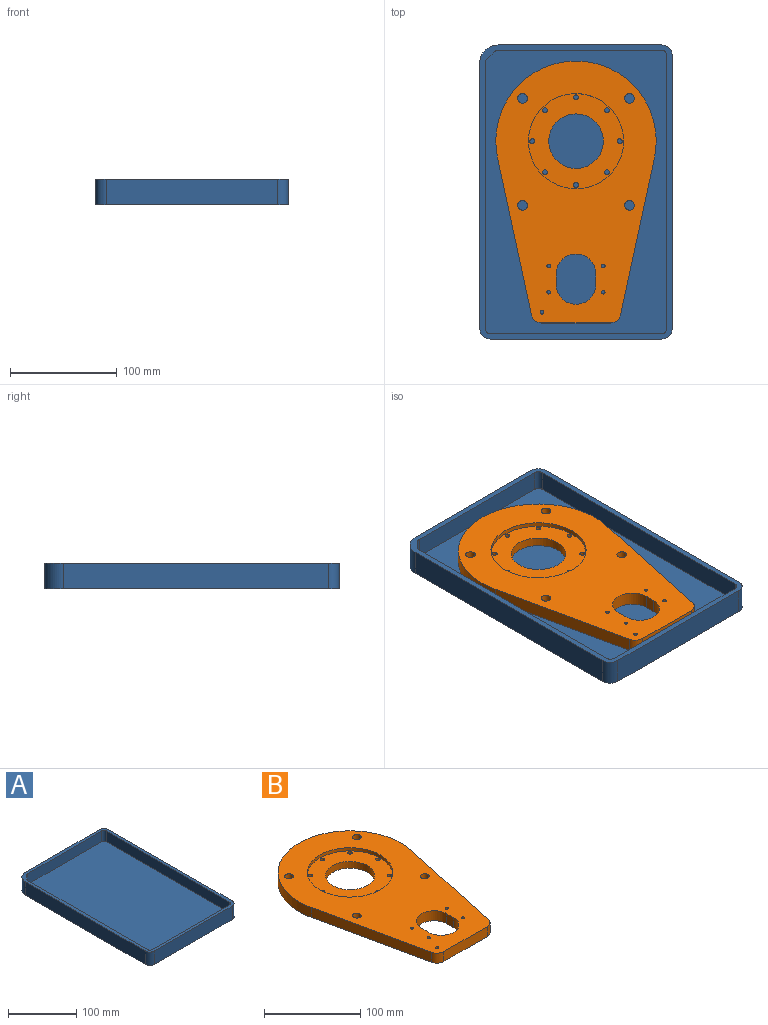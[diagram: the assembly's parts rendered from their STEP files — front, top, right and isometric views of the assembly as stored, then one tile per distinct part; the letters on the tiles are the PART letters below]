
ASSEMBLY  parts=2 mates=1
PART A: 21 faces, bbox 180x275x24 mm
  f0: plane 160x24mm, normal (0,-1,0), area 3840mm2, adj f1,f17,f18,f19
  f1: cylinder r=10mm len=24mm, axis (0,0,-1), area 377mm2, adj f0,f2,f18,f19
  f2: plane 255x24mm, normal (1,0,0), area 6120mm2, adj f1,f3,f18,f19
  f3: cylinder r=10mm len=24mm, axis (0,0,-1), area 377mm2, adj f2,f4,f18,f19
  f4: plane 152.93x24mm, normal (0,1,0), area 3670.3mm2, adj f3,f5,f18,f19
  f5: cylinder r=17.07mm len=24mm, axis (0,0,-1), area 643.6mm2, adj f4,f6,f18,f19
  f6: plane 247.93x24mm, normal (-1,0,0), area 5950.3mm2, adj f5,f17,f18,f19
  f7: cylinder r=5mm len=19mm, axis (0,0,-1), area 149.2mm2, adj f8,f16,f18,f20
  f8: plane 255x19mm, normal (-1,0,0), area 4845mm2, adj f7,f9,f18,f20
  f9: cylinder r=5mm len=19mm, axis (0,0,-1), area 149.2mm2, adj f8,f10,f18,f20
  f10: plane 160x19mm, normal (0,1,0), area 3040mm2, adj f9,f11,f18,f20
  f11: cylinder r=5mm len=19mm, axis (0,0,-1), area 149.2mm2, adj f10,f12,f18,f20
  f12: plane 247.93x19mm, normal (1,0,0), area 4710.6mm2, adj f11,f13,f18,f20
  f13: cylinder r=5mm len=19mm, axis (0,0,-1), area 74.6mm2, adj f12,f14,f18,f20
  f14: plane 19x7.07mm, normal (0.71,-0.71,0), area 190mm2, adj f13,f15,f18,f20
  f15: cylinder r=5mm len=19mm, axis (0,0,-1), area 74.6mm2, adj f14,f16,f18,f20
  f16: plane 152.93x19mm, normal (0,-1,0), area 2905.6mm2, adj f7,f15,f18,f20
  f17: cylinder r=10mm len=24mm, axis (0,0,-1), area 377mm2, adj f0,f6,f18,f19
  f18: plane 275x180mm, normal (0,0,1), area 4390.3mm2, adj f0,f1,f2,f3,f4,f5,f6,f7
  f19: plane 275x180mm, normal (0,0,-1), area 49373.1mm2, adj f0,f1,f2,f3,f4,f5,f6,f17
  f20: plane 265x170mm, normal (0,0,1), area 44982.8mm2, adj f7,f8,f9,f10,f11,f12,f13,f14
PART B: 48 faces, bbox 150x245x12.7 mm
  f0: cylinder r=2.25mm len=4.7mm, axis (0,0,-1), area 66.4mm2, adj f31,f46
  f1: cylinder r=2.25mm len=4.7mm, axis (0,0,-1), area 66.4mm2, adj f31,f44
  f2: cylinder r=2.25mm len=4.7mm, axis (0,0,-1), area 66.4mm2, adj f31,f42
  f3: cylinder r=2.25mm len=4.7mm, axis (0,0,-1), area 66.4mm2, adj f31,f40
  f4: cylinder r=2.25mm len=4.7mm, axis (0,0,-1), area 66.4mm2, adj f31,f38
  f5: cylinder r=2.25mm len=4.7mm, axis (0,0,-1), area 66.4mm2, adj f31,f36
  f6: cylinder r=2.25mm len=4.7mm, axis (0,0,-1), area 66.4mm2, adj f31,f34
  f7: cylinder r=2.25mm len=4.7mm, axis (0,0,-1), area 66.4mm2, adj f31,f32
  f8: plane 12.7x10mm, normal (1,0,0), area 127mm2, adj f9,f25,f28,f29
  f9: cylinder r=18.5mm len=37mm, axis (0,0,-1), area 738.1mm2, adj f8,f10,f28,f29
  f10: plane 12.7x10mm, normal (-1,0,0), area 127mm2, adj f9,f25,f28,f29
  f11: plane 146.27x31.6mm, normal (0.98,-0.21,0), area 1900.5mm2, adj f12,f26,f28,f29
  f12: cylinder r=75mm len=150mm, axis (0,0,-1), area 3397.7mm2, adj f11,f13,f28,f29
  f13: plane 146.27x31.6mm, normal (-0.98,-0.21,0), area 1900.5mm2, adj f12,f14,f28,f29
  f14: cylinder r=10mm len=12.7mm, axis (0,0,-1), area 172.5mm2, adj f13,f15,f28,f29
  f15: plane 63.86x12.7mm, normal (0,-1,0), area 811mm2, adj f14,f26,f28,f29
  f16: cylinder r=1.65mm len=12.7mm, axis (0,0,-1), area 131.7mm2, adj f28,f29
  f17: cylinder r=1.65mm len=12.7mm, axis (0,0,-1), area 131.7mm2, adj f28,f29
  f18: cylinder r=1.65mm len=12.7mm, axis (0,0,-1), area 131.7mm2, adj f28,f29
  f19: cylinder r=1.65mm len=12.7mm, axis (0,0,-1), area 131.7mm2, adj f28,f29
  f20: cylinder r=4.5mm len=12.7mm, axis (0,0,-1), area 359.1mm2, adj f28,f29
  f21: cylinder r=4.5mm len=12.7mm, axis (0,0,-1), area 359.1mm2, adj f28,f29
  f22: cylinder r=4.5mm len=12.7mm, axis (0,0,-1), area 359.1mm2, adj f28,f29
  f23: cylinder r=4.5mm len=12.7mm, axis (0,0,-1), area 359.1mm2, adj f28,f29
  f24: cylinder r=44.5mm len=89mm, axis (0,0,-1), area 1118.4mm2, adj f28,f31
  f25: cylinder r=18.5mm len=37mm, axis (0,0,-1), area 738.1mm2, adj f8,f10,f28,f29
  f26: cylinder r=10mm len=12.7mm, axis (0,0,-1), area 172.5mm2, adj f11,f15,f28,f29
  f27: cylinder r=1.65mm len=12.7mm, axis (0,0,-1), area 131.7mm2, adj f28,f29
  f28: plane 245x150mm, normal (0,0,1), area 20672.4mm2, adj f8,f9,f10,f11,f12,f13,f14,f15
  f29: plane 245x150mm, normal (0,0,-1), area 24423mm2, adj f8,f9,f10,f11,f12,f13,f14,f15
  f30: cylinder r=25.5mm len=51mm, axis (0,0,-1), area 1393.9mm2, adj f29,f31
  f31: plane 89x89mm, normal (0,0,1), area 4051.1mm2, adj f0,f1,f2,f3,f4,f5,f6,f7
  f32: plane 8.25x8.25mm, normal (0,0,-1), area 37.6mm2, adj f7,f33
  f33: cylinder r=4.12mm len=8.25mm, axis (0,0,-1), area 103.7mm2, adj f29,f32
  f34: plane 8.25x8.25mm, normal (0,0,-1), area 37.6mm2, adj f6,f35
  f35: cylinder r=4.12mm len=8.25mm, axis (0,0,-1), area 103.7mm2, adj f29,f34
  f36: plane 8.25x8.25mm, normal (0,0,-1), area 37.6mm2, adj f5,f37
  f37: cylinder r=4.12mm len=8.25mm, axis (0,0,-1), area 103.7mm2, adj f29,f36
  f38: plane 8.25x8.25mm, normal (0,0,-1), area 37.6mm2, adj f4,f39
  f39: cylinder r=4.12mm len=8.25mm, axis (0,0,-1), area 103.7mm2, adj f29,f38
  f40: plane 8.25x8.25mm, normal (0,0,-1), area 37.6mm2, adj f3,f41
  f41: cylinder r=4.12mm len=8.25mm, axis (0,0,-1), area 103.7mm2, adj f29,f40
  f42: plane 8.25x8.25mm, normal (0,0,-1), area 37.6mm2, adj f2,f43
  f43: cylinder r=4.12mm len=8.25mm, axis (0,0,-1), area 103.7mm2, adj f29,f42
  f44: plane 8.25x8.25mm, normal (0,0,-1), area 37.6mm2, adj f1,f45
  f45: cylinder r=4.12mm len=8.25mm, axis (0,0,-1), area 103.7mm2, adj f29,f44
  f46: plane 8.25x8.25mm, normal (0,0,-1), area 37.6mm2, adj f0,f47
  f47: cylinder r=4.12mm len=8.25mm, axis (0,0,-1), area 103.7mm2, adj f29,f46
PLACE A at identity
PLACE B t=(0,0,5)mm
MATE fastened B.f30 <-> A.f20  axis (0,0,1) through (0,0,5)mm
